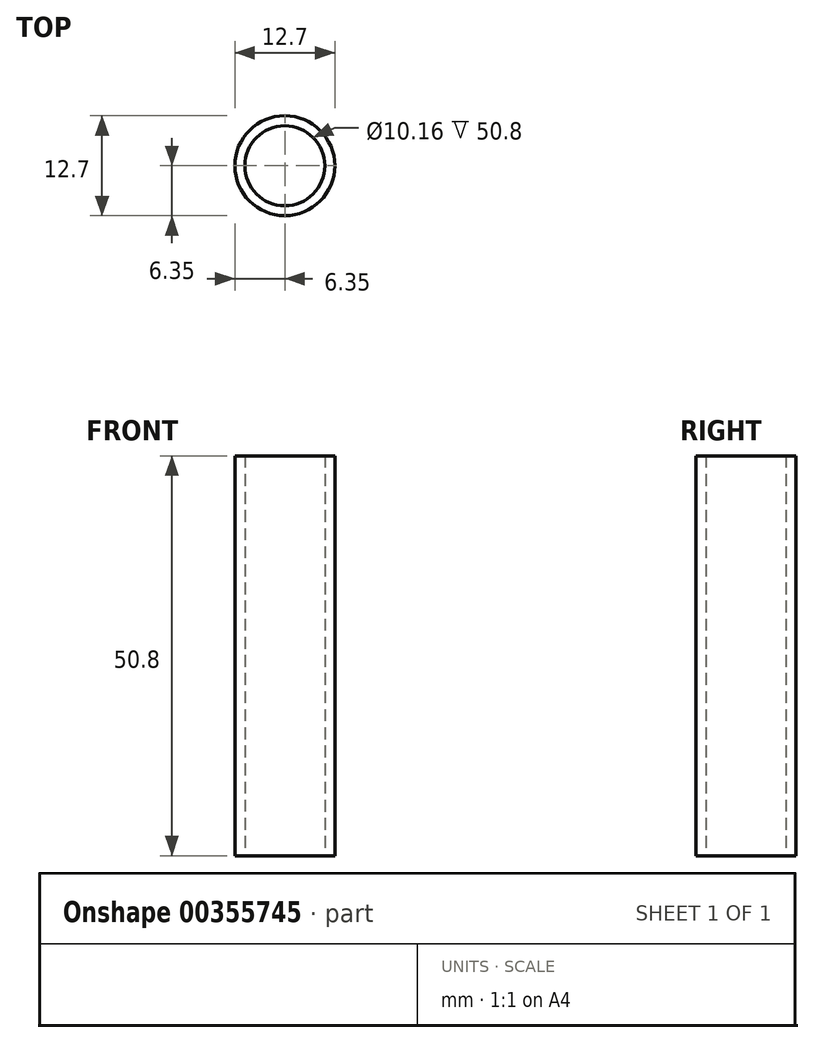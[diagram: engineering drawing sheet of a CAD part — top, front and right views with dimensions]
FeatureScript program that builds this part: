
annotation { "Feature Type Name" : "Feature", "Feature Type Description" : "" }
export const myFeature = defineFeature(function(context is Context, id is Id, definition is map)
    precondition{}
    {
        {
            var Q0;
            Q0=qCreatedBy(makeId("Top.planeOp"),FACE);
            var sketch = newSketch(context, id + "F0", { "sketchPlane" : qUnion([Q0])});
            skCircle(sketch, "E0", {"center": v(0, 0) * mm, "radius": 5.08 * mm});
            skCircle(sketch, "E1", {"center": v(0, 0) * mm, "radius": 6.35 * mm});
            skSolve(sketch);
        }
        {
            var Q0;
            Q0=qSketchRegion(id+"F0",true);
            extrude(context, id + "F1", {"entities" : qUnion([Q0]), "depth" : 50.8 * mm});
        }
    });
